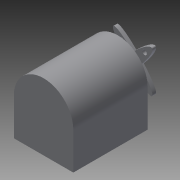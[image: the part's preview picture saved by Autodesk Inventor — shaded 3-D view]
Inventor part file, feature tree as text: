
AUTODESK INVENTOR PART (.ipt)
format: ipt  version: 2014 (Build 180170000, 170)  size: 144,896 bytes
history: native  units: mm
features: extrude x4, sketch x4
ambient origin geometry x8: Origin, YZ Plane, XZ Plane, XY Plane, X Axis, Y Axis, Z Axis, Center Point
bodies: Solid1 (feature_tree)
feature tree (8):
  extrude  "Extrusion1"  Depth=50.0mm TaperAngle=0.0deg
  extrude  "Extrusion2"  Depth=10.0mm TaperAngle=0.0deg
  extrude  "Extrusion3"  Depth=3.0mm
  extrude  "Extrusion4"  Depth=2.5mm
  sketch  "Sketch1"  dims[d0=40.0mm d2=50.0mm d3=0.0mm]
  sketch  "Sketch2"  dims[d4=7.5mm d5=10.0mm d6=0.0mm]
  sketch  "Sketch3"  dims[d7=3.0mm d8=3.0mm]
  sketch  "Sketch4"  dims[d9=3.0mm d10=3.0mm d11=2.5mm d12=0.0mm d13=2.5mm d14=0.0mm]
